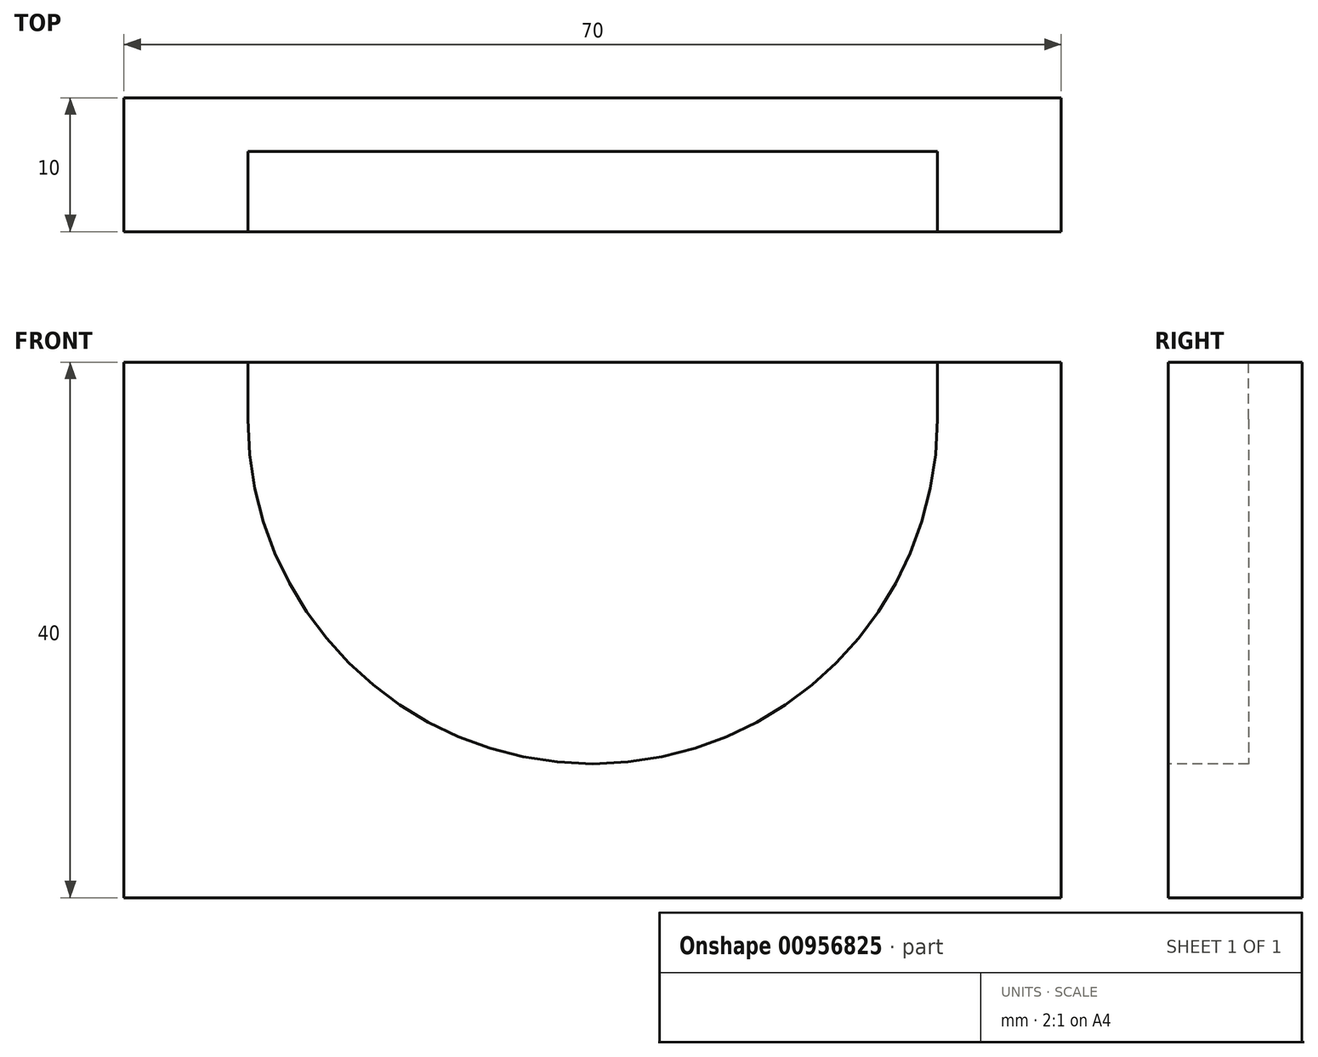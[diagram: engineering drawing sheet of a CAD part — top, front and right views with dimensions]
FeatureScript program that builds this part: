
annotation { "Feature Type Name" : "Feature", "Feature Type Description" : "" }
export const myFeature = defineFeature(function(context is Context, id is Id, definition is map)
    precondition{}
    {
        {
            var Q0;
            Q0=qCreatedBy(makeId("Front.planeOp"),FACE);
            var sketch = newSketch(context, id + "F0", { "sketchPlane" : qUnion([Q0])});
            skArc(sketch, "E0", {"start": v(-25.75, 0) * mm, "mid": v(0, -25.75) * mm, "end": v(25.75, 0) * mm});
            skLineSegment(sketch, "E1", {"start": v(0, -35.75) * mm, "end": v(-35, -35.75) * mm});
            skLineSegment(sketch, "E2", {"start": v(0, -35.75) * mm, "end": v(35, -35.75) * mm});
            skLineSegment(sketch, "E3", {"start": v(35, -35.75) * mm, "end": v(35, 4.25) * mm});
            skLineSegment(sketch, "E4", {"start": v(35, 4.25) * mm, "end": v(-35, 4.25) * mm});
            skLineSegment(sketch, "E5", {"start": v(-35, 4.25) * mm, "end": v(-35, -35.75) * mm});
            skLineSegment(sketch, "E6", {"start": v(-25.75, 0) * mm, "end": v(-25.75, 4.25) * mm});
            skLineSegment(sketch, "E7", {"start": v(25.75, 0) * mm, "end": v(25.75, 4.25) * mm});
            skSolve(sketch);
        }
        {
            var Q0;
            Q0=makeQuery(id+"F0.imprint","IMPRINT",FACE,{"disambiguationData":[TD([[makeQuery(id+"F0.imprint","IMPRINT",EDGE,{"derivedFrom":sQuery(id+"F0.wireOp",EDGE,"E0")}),-1.0]])]});
            var Q1;
            Q1=makeQuery(id+"F0.imprint","IMPRINT",FACE,{"disambiguationData":[TD([[makeQuery(id+"F0.imprint","IMPRINT",EDGE,{"derivedFrom":sQuery(id+"F0.wireOp",EDGE,"E0")}),1.0]])]});
            extrude(context, id + "F1", {"entities" : qUnion([Q0, Q1]), "oppositeDirection" : true, "depth" : 10 * mm, "offsetDistance" : 25 * mm});
        }
        {
            var Q0;
            Q0=makeQuery(id+"F0.imprint","IMPRINT",FACE,{"disambiguationData":[TD([[makeQuery(id+"F0.imprint","IMPRINT",EDGE,{"derivedFrom":sQuery(id+"F0.wireOp",EDGE,"E0")}),1.0]])]});
            extrude(context, id + "F2", {"entities" : qUnion([Q0]), "operationType" : NewBodyOperationType.REMOVE, "oppositeDirection" : true, "depth" : 6 * mm, "offsetDistance" : 25 * mm});
        }
    });
